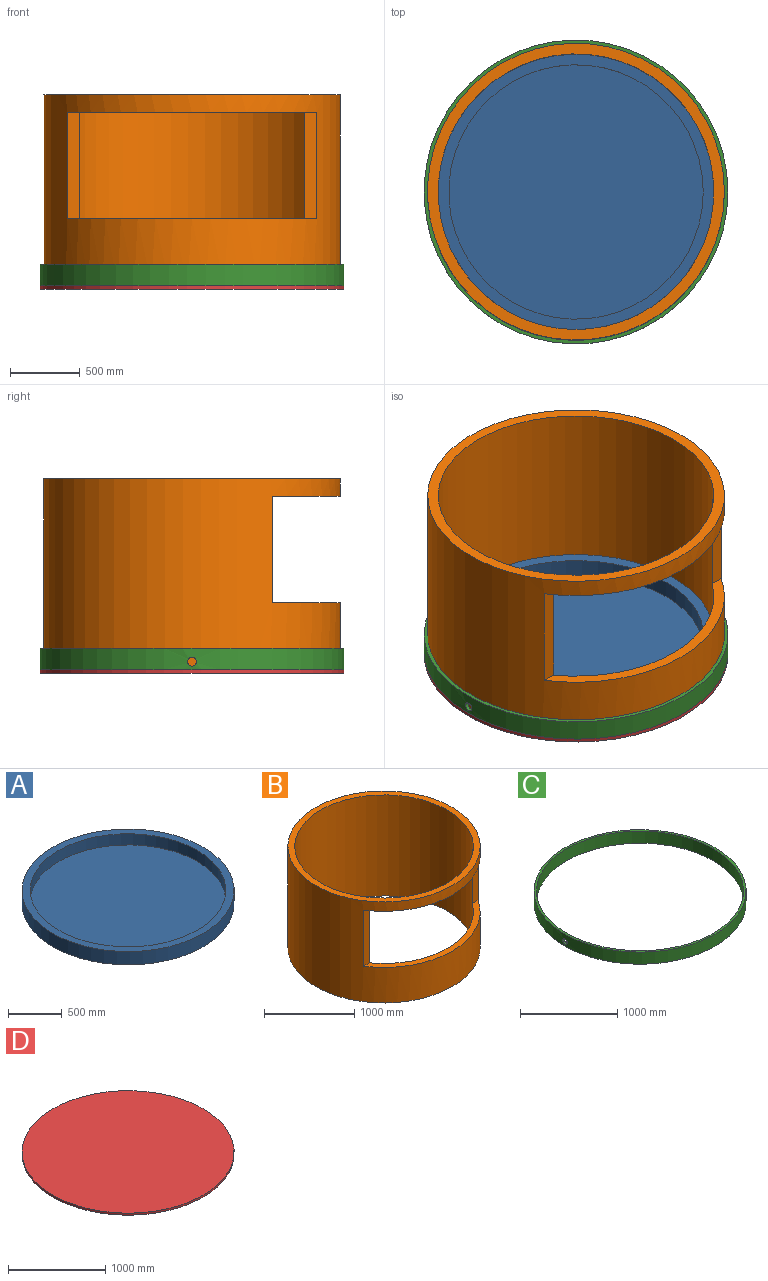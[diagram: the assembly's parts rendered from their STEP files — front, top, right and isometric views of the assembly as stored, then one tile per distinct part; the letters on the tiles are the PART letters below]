
ASSEMBLY  parts=4 mates=3
PART A: 5 faces, bbox 1981.2x1981.2x152.4 mm
  f0: cylinder r=914.4mm len=1828.8mm, axis (0,0,-1), area 729658.8mm2, adj f2,f4
  f1: cylinder r=990.6mm len=1981.2mm, axis (0,0,-1), area 948556.4mm2, adj f2,f3
  f2: plane 1981.2x1981.2mm, normal (0,0,1), area 456036.7mm2, adj f0,f1
  f3: plane 1981.2x1981.2mm, normal (0,0,-1), area 3082808.3mm2, adj f1
  f4: plane 1828.8x1828.8mm, normal (0,0,1), area 2626771.6mm2, adj f0
PART B: 8 faces, bbox 2133.6x2133.6x1371.6 mm
  f0: cylinder r=990.6mm len=1981.2mm, axis (0,0,-1), area 7103500.4mm2, adj f2,f3,f4,f5,f6,f7
  f1: cylinder r=1066.8mm len=2133.6mm, axis (0,0,-1), area 7568233.3mm2, adj f2,f3,f4,f5,f6,f7
  f2: plane 2133.6x2133.6mm, normal (0,0,1), area 492519.7mm2, adj f0,f1
  f3: plane 2133.6x2133.6mm, normal (0,0,-1), area 492519.7mm2, adj f0,f1
  f4: plane 1795.12x490.22mm, normal (0,0,-1), area 152971.1mm2, adj f0,f1,f6,f7
  f5: plane 1795.12x490.22mm, normal (0,0,1), area 152971.1mm2, adj f0,f1,f6,f7
  f6: plane 762x92.05mm, normal (0,-1,0), area 70144.9mm2, adj f0,f1,f4,f5
  f7: plane 762x92.05mm, normal (0,-1,0), area 70144.9mm2, adj f0,f1,f4,f5
PART C: 5 faces, bbox 2184.4x2184.4x152.4 mm
  f0: cylinder r=1066.8mm len=2133.6mm, axis (0,0,-1), area 1018335.9mm2, adj f2,f3,f4
  f1: cylinder r=1092.2mm len=2184.4mm, axis (0,0,-1), area 1042657.7mm2, adj f2,f3,f4
  f2: plane 2184.4x2184.4mm, normal (0,0,1), area 172280.5mm2, adj f0,f1
  f3: plane 2184.4x2184.4mm, normal (0,0,-1), area 172280.5mm2, adj f0,f1
  f4: cylinder r=31.75mm len=63.5mm, axis (-1,0,0), area 5068.2mm2, adj f0,f1
PART D: 3 faces, bbox 2184.4x2184.4x25.4 mm
  f0: cylinder r=1092.2mm len=2184.4mm, axis (0,0,1), area 174307.4mm2, adj f1,f2
  f1: plane 2184.4x2184.4mm, normal (0,0,-1), area 3747608.5mm2, adj f0
  f2: plane 2184.4x2184.4mm, normal (0,0,1), area 3747608.5mm2, adj f0
PLACE A t=(-3549.76,-2981.43,68.36)mm
PLACE B t=(-3549.76,-2981.43,68.36)mm
PLACE C t=(-3549.76,-2981.43,68.36)mm
PLACE D t=(-3549.76,-2981.43,68.36)mm
MATE fastened A.f1 <-> D.f0  axis (0,0,-1) through (-3549.76,-2981.43,68.36)mm
MATE fastened D.f0 <-> C.f0  axis (0,0,1) through (-3549.76,-2981.43,68.36)mm
MATE fastened B.f1 <-> D.f0  axis (0,0,-1) through (-3549.76,-2981.43,68.36)mm
